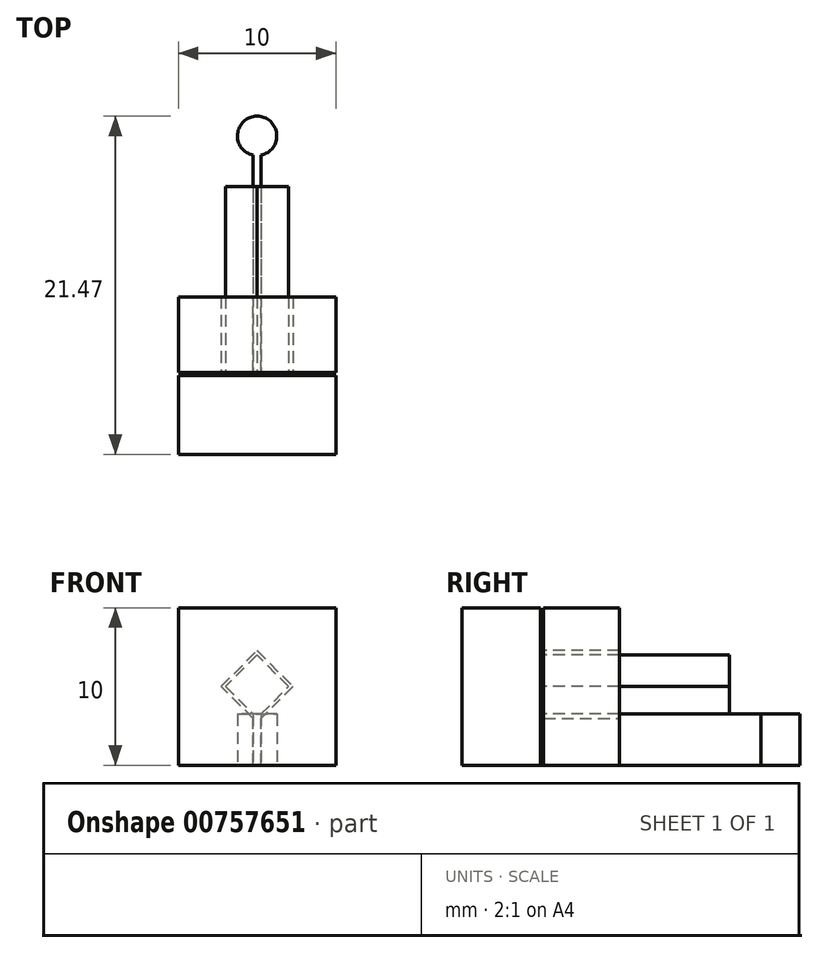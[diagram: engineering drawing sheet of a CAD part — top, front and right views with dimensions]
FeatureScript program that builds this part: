
annotation { "Feature Type Name" : "Feature", "Feature Type Description" : "" }
export const myFeature = defineFeature(function(context is Context, id is Id, definition is map)
    precondition{}
    {
        {
            var Q0;
            Q0=qCreatedBy(makeId("Right.planeOp"),FACE);
            var sketch = newSketch(context, id + "F0", { "sketchPlane" : qUnion([Q0])});
            skLineSegment(sketch, "E0.bottom", {"start": v(-10, 10) * mm, "end": v(-5, 10) * mm});
            skLineSegment(sketch, "E0.top", {"start": v(-10, 0) * mm, "end": v(-5, 0) * mm});
            skLineSegment(sketch, "E0.left", {"start": v(-10, 10) * mm, "end": v(-10, 0) * mm});
            skLineSegment(sketch, "E0.right", {"start": v(-5, 10) * mm, "end": v(-5, 0) * mm});
            skLineSegment(sketch, "E1.bottom", {"start": v(-5, 10) * mm, "end": v(0, 10) * mm});
            skLineSegment(sketch, "E1.top", {"start": v(-5, 0) * mm, "end": v(0, 0) * mm});
            skLineSegment(sketch, "E1.right", {"start": v(0, 10) * mm, "end": v(0, 0) * mm});
            skLineSegment(sketch, "E2", {"start": v(-5, 10) * mm, "end": v(-4.8, 10) * mm});
            skLineSegment(sketch, "E3", {"start": v(-4.8, 10) * mm, "end": v(-4.8, 0) * mm});
            skSolve(sketch);
        }
        {
            var Q0;
            Q0=makeQuery(id+"F0.imprint","IMPRINT",FACE,{"disambiguationData":[TD([[makeQuery(id+"F0.imprint","IMPRINT",EDGE,{"derivedFrom":sQuery(id+"F0.wireOp",EDGE,"E0.bottom")}),-1.0]])]});
            extrude(context, id + "F1", {"entities" : qUnion([Q0]), "depth" : 10 * mm, "offsetDistance" : 25 * mm});
        }
        {
            var Q0;
            {var subQ2=sQuery(id+"F0.wireOp",EDGE,"E1.right");Q0=makeQuery(id+"F0.imprint","IMPRINT",FACE,{"disambiguationData":[TD([[makeQuery(id+"F0.imprint","IMPRINT",EDGE,{"derivedFrom":subQ2}),-1.0]])]});}
            extrude(context, id + "F2", {"entities" : qUnion([Q0]), "depth" : 10 * mm, "offsetDistance" : 25 * mm});
        }
        {
            var Q0;
            Q0=makeQuery(id+"F1.opExtrude","SWEPT_FACE",FACE,{"disambiguationData":[OSD([sQuery(id+"F0.wireOp",EDGE,"E0.right")])]});
            var sketch = newSketch(context, id + "F3", { "sketchPlane" : qUnion([Q0])});
            skLineSegment(sketch, "E4", {"start": v(0, 5) * mm, "end": v(-3, 5) * mm, "construction": true});
            skLineSegment(sketch, "E5", {"start": v(-10, 5) * mm, "end": v(-7, 5) * mm, "construction": true});
            skLineSegment(sketch, "E6", {"start": v(-3, 5) * mm, "end": v(-7, 5) * mm, "construction": true});
            skLineSegment(sketch, "E7", {"start": v(-5, 5) * mm, "end": v(-5, 7) * mm, "construction": true});
            skLineSegment(sketch, "E8", {"start": v(-5, 5) * mm, "end": v(-5, 3) * mm, "construction": true});
            skLineSegment(sketch, "E9", {"start": v(-5, 3) * mm, "end": v(-7, 5) * mm});
            skLineSegment(sketch, "E10", {"start": v(-7, 5) * mm, "end": v(-5, 7) * mm});
            skLineSegment(sketch, "E11", {"start": v(-5, 7) * mm, "end": v(-3, 5) * mm});
            skLineSegment(sketch, "E12", {"start": v(-3, 5) * mm, "end": v(-5, 3) * mm});
            skLineSegment(sketch, "E13.0", {"start": v(-5, 2.72) * mm, "end": v(-7.28, 5) * mm});
            skLineSegment(sketch, "E13.1", {"start": v(-2.72, 5) * mm, "end": v(-5, 2.72) * mm});
            skLineSegment(sketch, "E13.2", {"start": v(-5, 7.28) * mm, "end": v(-2.72, 5) * mm});
            skLineSegment(sketch, "E13.3", {"start": v(-7.28, 5) * mm, "end": v(-5, 7.28) * mm});
            skSolve(sketch);
        }
        {
            var Q0;
            Q0=makeQuery(id+"F3.imprint","IMPRINT",FACE,{"disambiguationData":[TD([[makeQuery(id+"F3.imprint","IMPRINT",EDGE,{"derivedFrom":sQuery(id+"F3.wireOp",EDGE,"E9")}),1.0]])]});
            var Q1;
            Q1=makeQuery(id+"F3.imprint","IMPRINT",FACE,{"disambiguationData":[TD([[makeQuery(id+"F3.imprint","IMPRINT",EDGE,{"derivedFrom":sQuery(id+"F3.wireOp",EDGE,"E9")}),-1.0]])]});
            extrude(context, id + "F4", {"entities" : qUnion([Q0, Q1]), "operationType" : NewBodyOperationType.REMOVE, "oppositeDirection" : true, "depth" : -10 * mm, "offsetDistance" : 25 * mm});
        }
        {
            var Q0;
            Q0=makeQuery(id+"F3.imprint","IMPRINT",FACE,{"disambiguationData":[TD([[makeQuery(id+"F3.imprint","IMPRINT",EDGE,{"derivedFrom":sQuery(id+"F3.wireOp",EDGE,"E9")}),-1.0]])]});
            extrude(context, id + "F5", {"entities" : qUnion([Q0]), "operationType" : NewBodyOperationType.ADD, "depth" : 12 * mm, "offsetDistance" : 25 * mm});
        }
        {
            var Q0;
            Q0=makeQuery(id+"F5.opExtrude","CAP_FACE",FACE,{"disambiguationData":[OSD([sQuery(id+"F3.wireOp",EDGE,"E9"),sQuery(id+"F3.wireOp",EDGE,"E10"),sQuery(id+"F3.wireOp",EDGE,"E11"),sQuery(id+"F3.wireOp",EDGE,"E12")])],"isStart":false});
            var sketch = newSketch(context, id + "F6", { "sketchPlane" : qUnion([Q0])});
            skLineSegment(sketch, "E14.right", {"start": v(0, 3.97) * mm, "end": v(0, 4.47) * mm});
            skLineSegment(sketch, "E15", {"start": v(-5.25, 3.25) * mm, "end": v(-5.25, 0) * mm});
            skLineSegment(sketch, "E16", {"start": v(-4.75, 3.25) * mm, "end": v(-4.75, 0) * mm});
            skLineSegment(sketch, "E17", {"start": v(-4.75, 3.25) * mm, "end": v(-5.25, 3.25) * mm});
            skPoint(sketch, "E18", {"position": v(-5, 3.25) * mm});
            skLineSegment(sketch, "E19", {"start": v(-5.25, 0) * mm, "end": v(-4.75, 0) * mm});
            skSolve(sketch);
        }
        {
            var Q0;
            {var subQ4=sQuery(id+"F6.wireOp",EDGE,"E15");Q0=makeQuery(id+"F6.imprint","IMPRINT",FACE,{"disambiguationData":[TD([[makeQuery(id+"F6.imprint","IMPRINT",EDGE,{"derivedFrom":subQ4}),1.0]])]});}
            var Q1;
            {var subQ0=sQuery(id+"F6.wireOp",EDGE,"E17");Q1=makeQuery(id+"F6.imprint","IMPRINT",FACE,{"disambiguationData":[TD([[makeQuery(id+"F6.imprint","IMPRINT",EDGE,{"derivedFrom":subQ0}),1.0]])]});}
            var Q2;
            Q2=makeQuery(id+"F1.opExtrude","SWEPT_FACE",FACE,{"disambiguationData":[OSD([sQuery(id+"F0.wireOp",EDGE,"E0.right")])]});
            extrude(context, id + "F7", {"entities" : qUnion([Q0, Q1]), "operationType" : NewBodyOperationType.ADD, "depth" : 2 * mm, "offsetDistance" : 25 * mm, "hasSecondDirection" : true, "secondDirectionBound" : SecondDirectionBoundingType.UP_TO_SURFACE, "secondDirectionOppositeDirection" : true, "secondDirectionDepth" : 4 * mm, "secondDirectionBoundEntityFace" : qUnion([Q2])});
        }
        {
            var Q0;
            Q0=makeQuery(id+"F7.boolean.opBoolean","MERGE",FACE,{"derivedFrom":[makeQuery(id+"F1.opExtrude","SWEPT_FACE",FACE,{"disambiguationData":[OSD([sQuery(id+"F0.wireOp",EDGE,"E0.top")])]}),makeQuery(id+"F7.opExtrude","SWEPT_FACE",FACE,{"disambiguationData":[OSD([sQuery(id+"F6.wireOp",EDGE,"E19")])]})]});
            var sketch = newSketch(context, id + "F8", { "sketchPlane" : qUnion([Q0])});
            skLineSegment(sketch, "E20", {"start": v(5, -9) * mm, "end": v(5, -10.22) * mm, "construction": true});
            skCircle(sketch, "E21", {"center": v(5, -10.22) * mm, "radius": 1.25 * mm});
            skSolve(sketch);
        }
        {
            var Q0;
            {var subQ1=sQuery(id+"F6.wireOp",EDGE,"E19");var subQ2=makeQuery(id+"F7.opExtrude","CAP_EDGE",EDGE,{"disambiguationData":[OSD([subQ1])],"isStart":false});Q0=makeQuery(id+"F8.imprint","IMPRINT",FACE,{"disambiguationData":[TD([[makeQuery(id+"F8.imprint","IMPRINT",EDGE,{"derivedFrom":subQ2}),1.0]])]});}
            var Q1;
            Q1=makeQuery(id+"F7.opExtrude","SWEPT_FACE",FACE,{"disambiguationData":[OSD([sQuery(id+"F6.wireOp",EDGE,"E17")])]});
            extrude(context, id + "F9", {"entities" : qUnion([Q0]), "operationType" : NewBodyOperationType.ADD, "endBound" : BoundingType.UP_TO_SURFACE, "oppositeDirection" : true, "depth" : -3.5 * mm, "endBoundEntityFace" : qUnion([Q1]), "offsetDistance" : 25 * mm});
        }
    });
